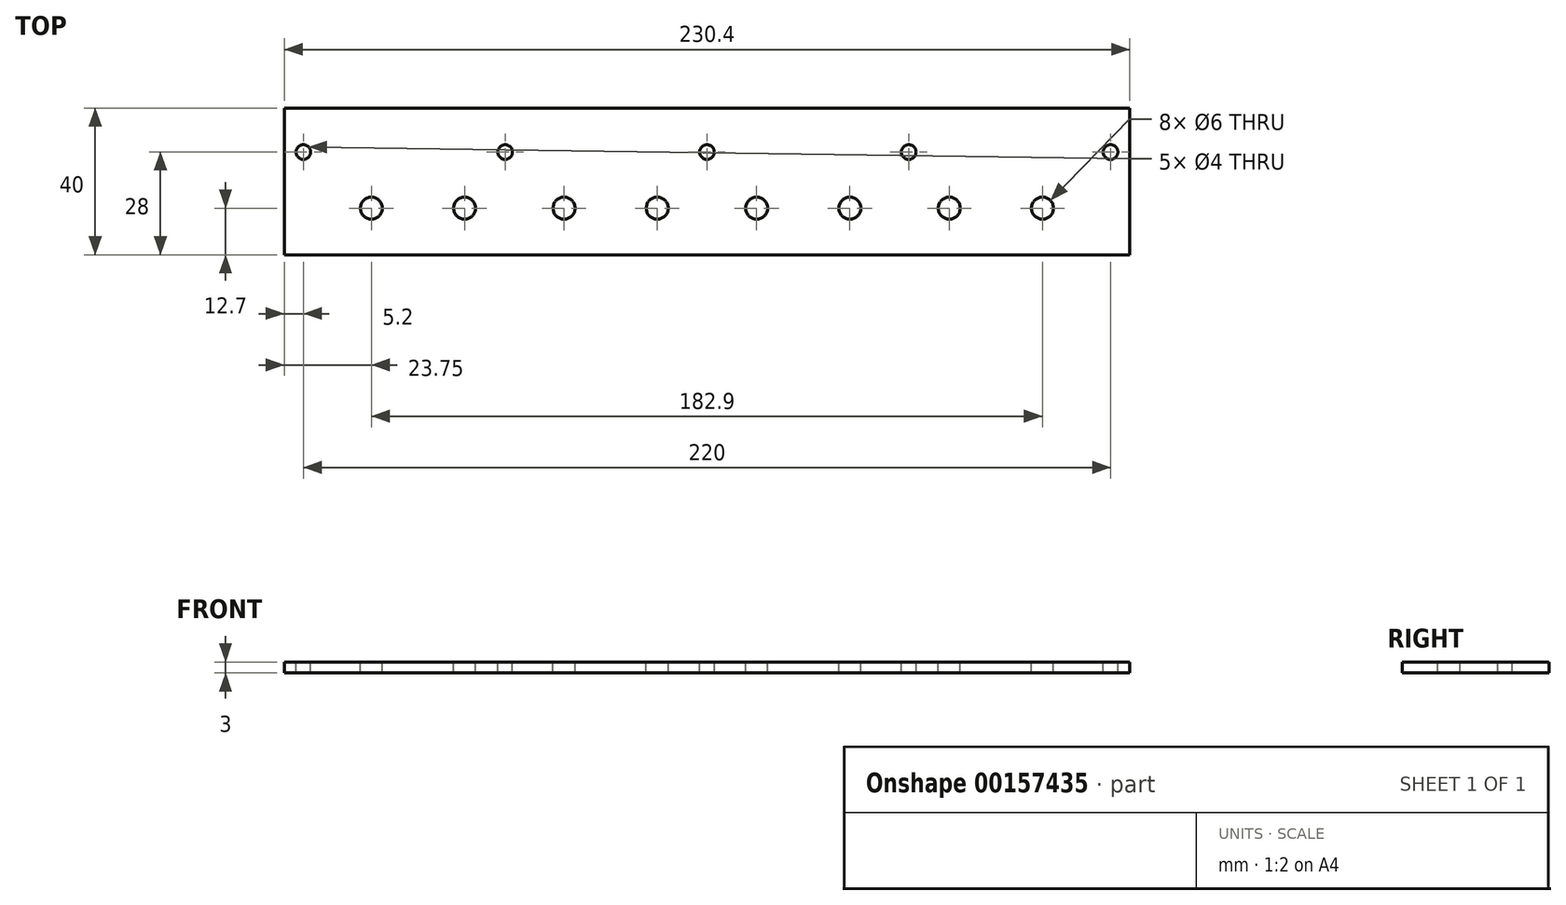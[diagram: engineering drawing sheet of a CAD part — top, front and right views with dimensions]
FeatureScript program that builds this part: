
annotation { "Feature Type Name" : "Feature", "Feature Type Description" : "" }
export const myFeature = defineFeature(function(context is Context, id is Id, definition is map)
    precondition{}
    {
        {
            var Q0;
            Q0=qCreatedBy(makeId("Top.planeOp"),FACE);
            var sketch = newSketch(context, id + "F0", { "sketchPlane" : qUnion([Q0])});
            skLineSegment(sketch, "E0.bottom", {"start": v(0, 0) * mm, "end": v(230.4, 0) * mm});
            skLineSegment(sketch, "E0.top", {"start": v(0, 40) * mm, "end": v(230.4, 40) * mm});
            skLineSegment(sketch, "E0.left", {"start": v(0, 0) * mm, "end": v(0, 40) * mm});
            skLineSegment(sketch, "E0.right", {"start": v(230.4, 0) * mm, "end": v(230.4, 40) * mm});
            skSolve(sketch);
        }
        {
            var Q0;
            Q0=qSketchRegion(id+"F0",true);
            extrude(context, id + "F1", {"entities" : qUnion([Q0]), "depth" : 3 * mm});
        }
        {
            var Q0;
            Q0=makeQuery(id+"F1.opExtrude","CAP_FACE",FACE,{"disambiguationData":[OSD([sQuery(id+"F0.wireOp",EDGE,"E0.bottom"),sQuery(id+"F0.wireOp",EDGE,"E0.top"),sQuery(id+"F0.wireOp",EDGE,"E0.left"),sQuery(id+"F0.wireOp",EDGE,"E0.right")])],"isStart":false});
            var sketch = newSketch(context, id + "F2", { "sketchPlane" : qUnion([Q0])});
            skCircle(sketch, "E1", {"center": v(5.2, 28) * mm, "radius": 2 * mm});
            skCircle(sketch, "E2.1.0.0", {"center": v(60.2, 28) * mm, "radius": 2 * mm});
            skCircle(sketch, "E2.2.0.0", {"center": v(115.2, 28) * mm, "radius": 2 * mm});
            skCircle(sketch, "E2.3.0.0", {"center": v(170.2, 28) * mm, "radius": 2 * mm});
            skCircle(sketch, "E2.4.0.0", {"center": v(225.2, 28) * mm, "radius": 2 * mm});
            skLineSegment(sketch, "E2.direction1", {"start": v(5.2, 28) * mm, "end": v(60.2, 28) * mm, "construction": true});
            skSolve(sketch);
        }
        {
            var Q0;
            Q0=qSketchRegion(id+"F2",true);
            extrude(context, id + "F3", {"entities" : qUnion([Q0]), "operationType" : NewBodyOperationType.REMOVE, "endBound" : BoundingType.THROUGH_ALL, "oppositeDirection" : true, "depth" : 25 * mm});
        }
        {
            var Q0;
            Q0=makeQuery(id+"F1.opExtrude","CAP_FACE",FACE,{"disambiguationData":[OSD([sQuery(id+"F0.wireOp",EDGE,"E0.bottom"),sQuery(id+"F0.wireOp",EDGE,"E0.top"),sQuery(id+"F0.wireOp",EDGE,"E0.left"),sQuery(id+"F0.wireOp",EDGE,"E0.right")])],"isStart":false});
            var sketch = newSketch(context, id + "F4", { "sketchPlane" : qUnion([Q0])});
            skCircle(sketch, "E3", {"center": v(23.75, 12.7) * mm, "radius": 3 * mm});
            skCircle(sketch, "E4", {"center": v(49.15, 12.7) * mm, "radius": 3 * mm});
            skCircle(sketch, "E5.1.0.0", {"center": v(76.25, 12.7) * mm, "radius": 3 * mm});
            skCircle(sketch, "E5.1.0.1", {"center": v(101.65, 12.7) * mm, "radius": 3 * mm});
            skCircle(sketch, "E5.2.0.0", {"center": v(128.75, 12.7) * mm, "radius": 3 * mm});
            skCircle(sketch, "E5.2.0.1", {"center": v(154.15, 12.7) * mm, "radius": 3 * mm});
            skCircle(sketch, "E5.3.0.0", {"center": v(181.25, 12.7) * mm, "radius": 3 * mm});
            skCircle(sketch, "E5.3.0.1", {"center": v(206.65, 12.7) * mm, "radius": 3 * mm});
            skLineSegment(sketch, "E5.direction1", {"start": v(23.75, 12.7) * mm, "end": v(76.25, 12.7) * mm, "construction": true});
            skSolve(sketch);
        }
        {
            var Q0;
            Q0=qSketchRegion(id+"F4",true);
            extrude(context, id + "F5", {"entities" : qUnion([Q0]), "operationType" : NewBodyOperationType.REMOVE, "endBound" : BoundingType.THROUGH_ALL, "oppositeDirection" : true, "depth" : 25 * mm});
        }
    });
